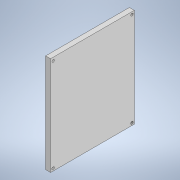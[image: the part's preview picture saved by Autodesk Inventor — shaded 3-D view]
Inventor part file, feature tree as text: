
AUTODESK INVENTOR PART (.ipt)
format: ipt  version: 2021 (Build 250183000, 183)  size: 122,368 bytes
history: native  units: mm
features: extrude x2, sketch x2
ambient origin geometry x8: Origin, YZ Plane, XZ Plane, XY Plane, X Axis, Y Axis, Z Axis, Center Point
bodies: Solid1 (feature_tree)
feature tree (4):
  extrude  "Extrusion1"  Depth=85.0mm
  extrude  "Extrusion2"  Depth=5.0mm TaperAngle=0.0deg
  sketch  "Sketch1"  dims[d0=100.0mm d1=85.0mm]
  sketch  "Sketch2"  dims[d2=100.0mm d3=5.0mm d4=0.0mm d5=2.5mm d6=2.5mm d7=2.5mm d8=2.5mm d9=2.51mm d10=2.5mm d11=2.5mm d12=2.5mm d13=2.51mm d14=2.51mm d15=2.5mm d16=2.5mm d17=2.5mm d18=2.5mm d19=2.51mm d20=2.5mm d21=2.5mm d22=2.51mm d23=4.8mm d24=0.0mm]
